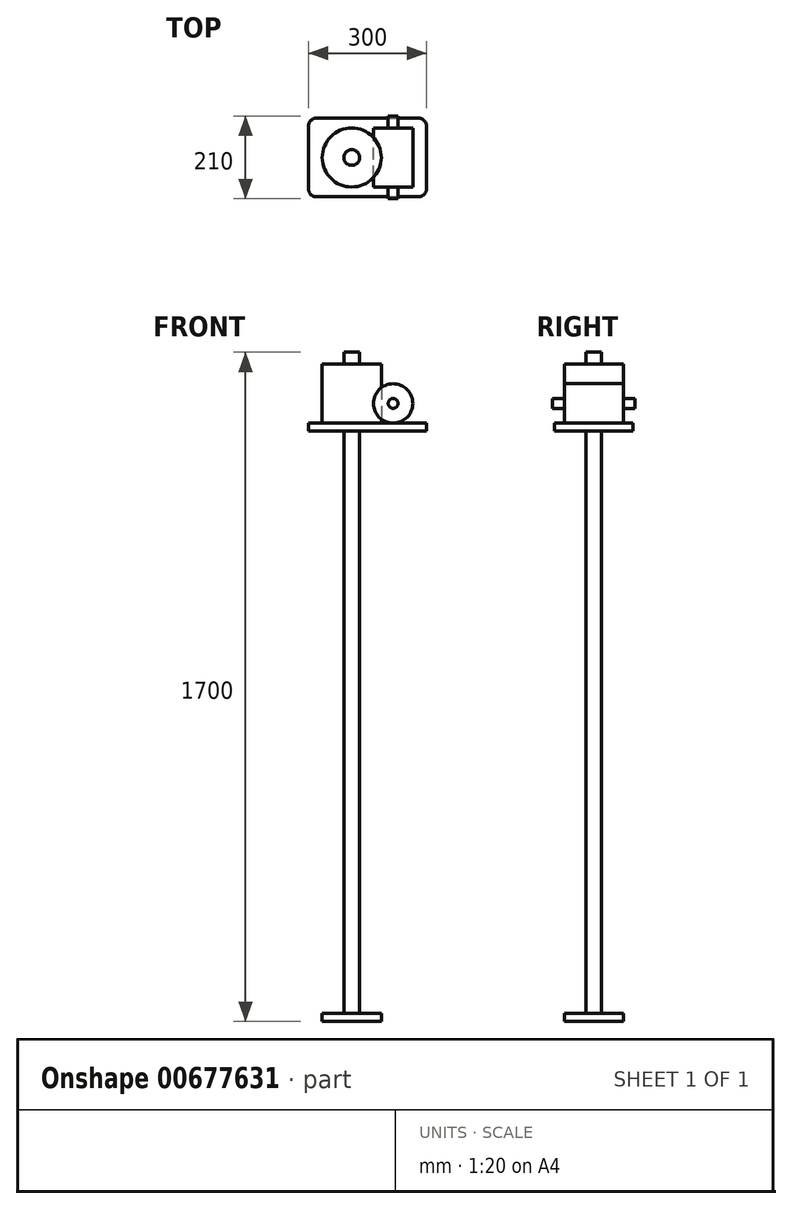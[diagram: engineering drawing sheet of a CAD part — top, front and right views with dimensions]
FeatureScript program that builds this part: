
annotation { "Feature Type Name" : "Feature", "Feature Type Description" : "" }
export const myFeature = defineFeature(function(context is Context, id is Id, definition is map)
    precondition{}
    {
        {
            var Q0;
            Q0=qCreatedBy(makeId("Top.planeOp"),FACE);
            var sketch = newSketch(context, id + "F0", { "sketchPlane" : qUnion([Q0])});
            skLineSegment(sketch, "E0.bottom", {"start": v(-150, -100) * mm, "end": v(150, -100) * mm});
            skLineSegment(sketch, "E0.top", {"start": v(-150, 100) * mm, "end": v(150, 100) * mm});
            skLineSegment(sketch, "E0.left", {"start": v(-150, -100) * mm, "end": v(-150, 100) * mm});
            skLineSegment(sketch, "E0.right", {"start": v(150, -100) * mm, "end": v(150, 100) * mm});
            skPoint(sketch, "E0.middle", {"position": v(0, 0) * mm});
            skSolve(sketch);
        }
        {
            var Q0;
            Q0=qSketchRegion(id+"F0",true);
            extrude(context, id + "F1", {"entities" : qUnion([Q0]), "depth" : 20 * mm, "offsetDistance" : 25 * mm});
        }
        {
            var Q0;
            Q0=makeQuery(id+"F1.opExtrude","CAP_FACE",FACE,{"disambiguationData":[OSD([sQuery(id+"F0.wireOp",EDGE,"E0.bottom"),sQuery(id+"F0.wireOp",EDGE,"E0.top"),sQuery(id+"F0.wireOp",EDGE,"E0.left"),sQuery(id+"F0.wireOp",EDGE,"E0.right")])],"isStart":false});
            var sketch = newSketch(context, id + "F2", { "sketchPlane" : qUnion([Q0])});
            skCircle(sketch, "E1", {"center": v(-40, 0) * mm, "radius": 75 * mm});
            skSolve(sketch);
        }
        {
            var Q0;
            Q0=makeQuery(id+"F2.imprint","IMPRINT",FACE,{"disambiguationData":[TD([[makeQuery(id+"F2.imprint","IMPRINT",EDGE,{"derivedFrom":sQuery(id+"F2.wireOp",EDGE,"E1")}),1.0]])]});
            extrude(context, id + "F3", {"entities" : qUnion([Q0]), "operationType" : NewBodyOperationType.ADD, "depth" : 150 * mm, "offsetDistance" : 25 * mm});
        }
        {
            var Q0;
            Q0=qCreatedBy(makeId("Front.planeOp"),FACE);
            var sketch = newSketch(context, id + "F4", { "sketchPlane" : qUnion([Q0])});
            skCircle(sketch, "E2", {"center": v(65.07, 70) * mm, "radius": 50 * mm});
            skSolve(sketch);
        }
        {
            var Q0;
            Q0=makeQuery(id+"F4.imprint","IMPRINT",FACE,{"disambiguationData":[TD([[makeQuery(id+"F4.imprint","IMPRINT",EDGE,{"derivedFrom":sQuery(id+"F4.wireOp",EDGE,"E2")}),1.0]])]});
            extrude(context, id + "F5", {"entities" : qUnion([Q0]), "endBound" : BoundingType.SYMMETRIC, "depth" : 150 * mm, "offsetDistance" : 25 * mm});
        }
        {
            var Q0;
            Q0=makeQuery(id+"F5.opExtrude","CAP_FACE",FACE,{"disambiguationData":[OSD([sQuery(id+"F4.wireOp",EDGE,"E2")])],"isStart":false});
            var sketch = newSketch(context, id + "F6", { "sketchPlane" : qUnion([Q0])});
            skCircle(sketch, "E3", {"center": v(65.07, 70) * mm, "radius": 12.5 * mm});
            skSolve(sketch);
        }
        {
            var Q0;
            Q0=makeQuery(id+"F6.imprint","IMPRINT",FACE,{"disambiguationData":[TD([[makeQuery(id+"F6.imprint","IMPRINT",EDGE,{"derivedFrom":sQuery(id+"F6.wireOp",EDGE,"E3")}),1.0]])]});
            var Q1;
            Q1=sQuery(id+"F6.wireOp",EDGE,"E3");
            extrude(context, id + "F7", {"entities" : qUnion([Q0]), "operationType" : NewBodyOperationType.ADD, "surfaceEntities" : qUnion([Q1]), "depth" : 30 * mm, "offsetDistance" : 25 * mm, "hasSecondDirection" : true, "secondDirectionOppositeDirection" : true, "secondDirectionDepth" : 180 * mm});
        }
        {
            var Q0;
            Q0=makeQuery(id+"F1.opExtrude","CAP_FACE",FACE,{"disambiguationData":[OSD([sQuery(id+"F0.wireOp",EDGE,"E0.bottom"),sQuery(id+"F0.wireOp",EDGE,"E0.top"),sQuery(id+"F0.wireOp",EDGE,"E0.left"),sQuery(id+"F0.wireOp",EDGE,"E0.right")])],"isStart":true});
            var sketch = newSketch(context, id + "F8", { "sketchPlane" : qUnion([Q0])});
            skCircle(sketch, "E4", {"center": v(-40, 0) * mm, "radius": 20 * mm});
            skSolve(sketch);
        }
        {
            var Q0;
            Q0=makeQuery(id+"F8.imprint","IMPRINT",FACE,{"disambiguationData":[TD([[makeQuery(id+"F8.imprint","IMPRINT",EDGE,{"derivedFrom":sQuery(id+"F8.wireOp",EDGE,"E4")}),1.0]])]});
            var Q1;
            Q1=sQuery(id+"F8.wireOp",EDGE,"E4");
            extrude(context, id + "F9", {"entities" : qUnion([Q0]), "operationType" : NewBodyOperationType.ADD, "surfaceEntities" : qUnion([Q1]), "depth" : 1500 * mm, "offsetDistance" : 25 * mm, "hasSecondDirection" : true, "secondDirectionOppositeDirection" : true, "secondDirectionDepth" : 200 * mm});
        }
        {
            var Q0;
            Q0=makeQuery(id+"F9.opExtrude","CAP_FACE",FACE,{"disambiguationData":[OSD([sQuery(id+"F8.wireOp",EDGE,"E4")])],"isStart":false});
            var sketch = newSketch(context, id + "F10", { "sketchPlane" : qUnion([Q0])});
            skCircle(sketch, "E5", {"center": v(-40, 0) * mm, "radius": 75 * mm});
            skSolve(sketch);
        }
        {
            var Q0;
            Q0=qSketchRegion(id+"F10",true);
            extrude(context, id + "F11", {"entities" : qUnion([Q0]), "operationType" : NewBodyOperationType.ADD, "oppositeDirection" : true, "depth" : 20 * mm, "offsetDistance" : 25 * mm});
        }
        {
            var Q0;
            Q0=makeQuery(id+"F1.opExtrude","SWEPT_EDGE",EDGE,{"disambiguationData":[OSD([sQuery(id+"F0.wireOp",EDGE,"E0.top"),sQuery(id+"F0.wireOp",EDGE,"E0.right")])]});
            var Q1;
            Q1=makeQuery(id+"F1.opExtrude","SWEPT_EDGE",EDGE,{"disambiguationData":[OSD([sQuery(id+"F0.wireOp",EDGE,"E0.bottom"),sQuery(id+"F0.wireOp",EDGE,"E0.right")])]});
            var Q2;
            Q2=makeQuery(id+"F1.opExtrude","SWEPT_EDGE",EDGE,{"disambiguationData":[OSD([sQuery(id+"F0.wireOp",EDGE,"E0.bottom"),sQuery(id+"F0.wireOp",EDGE,"E0.left")])]});
            var Q3;
            Q3=makeQuery(id+"F1.opExtrude","SWEPT_EDGE",EDGE,{"disambiguationData":[OSD([sQuery(id+"F0.wireOp",EDGE,"E0.top"),sQuery(id+"F0.wireOp",EDGE,"E0.left")])]});
            fillet(context, id + "F12", {"entities" : qUnion([Q0, Q1, Q2, Q3]), "radius" : 20 * mm, "tangentPropagation" : true, "allowEdgeOverflow" : false});
        }
    });
